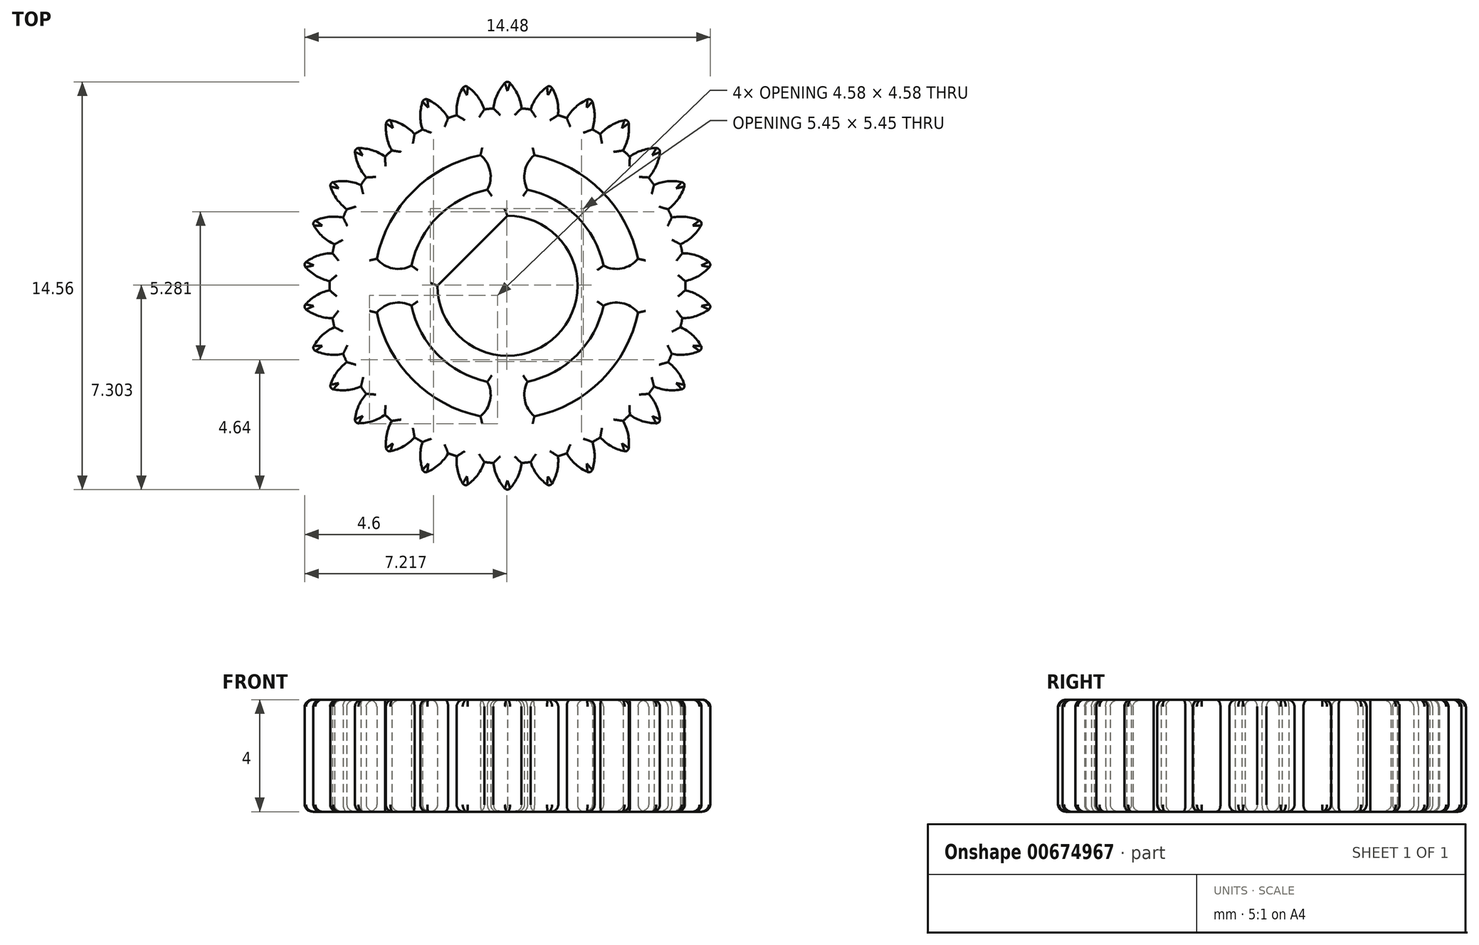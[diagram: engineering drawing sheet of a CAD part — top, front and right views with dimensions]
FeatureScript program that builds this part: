
annotation { "Feature Type Name" : "Feature", "Feature Type Description" : "" }
export const myFeature = defineFeature(function(context is Context, id is Id, definition is map)
    precondition{}
    {
        {
            var Q0;
            Q0=qCreatedBy(makeId("Top.planeOp"),FACE);
            var sketch = newSketch(context, id + "F0", { "sketchPlane" : qUnion([Q0])});
            skCircle(sketch, "E0", {"center": v(0, 0) * mm, "radius": 6.35 * mm});
            skCircle(sketch, "E1", {"center": v(0, 0) * mm, "radius": 4.76 * mm});
            skCircle(sketch, "E2", {"center": v(0, 0) * mm, "radius": 2.5 * mm});
            skCircle(sketch, "E3", {"center": v(0, 0) * mm, "radius": 3.5 * mm});
            skArc(sketch, "E4", {"start": v(-0.72, 3.43) * mm, "mid": v(-0.62, 4.09) * mm, "end": v(-0.96, 4.66) * mm});
            skLineSegment(sketch, "E5", {"start": v(0, 4.76) * mm, "end": v(0, 3.5) * mm});
            skArc(sketch, "E6.MirrorCS", {"start": v(0.72, 3.43) * mm, "mid": v(0.62, 4.09) * mm, "end": v(0.96, 4.66) * mm});
            skArc(sketch, "E7.1.0", {"start": v(-3.43, -0.72) * mm, "mid": v(-4.09, -0.62) * mm, "end": v(-4.66, -0.96) * mm});
            skArc(sketch, "E7.1.1", {"start": v(-3.43, 0.72) * mm, "mid": v(-4.09, 0.62) * mm, "end": v(-4.66, 0.96) * mm});
            skArc(sketch, "E7.2.0", {"start": v(0.72, -3.43) * mm, "mid": v(0.62, -4.09) * mm, "end": v(0.96, -4.66) * mm});
            skArc(sketch, "E7.2.1", {"start": v(-0.72, -3.43) * mm, "mid": v(-0.62, -4.09) * mm, "end": v(-0.96, -4.66) * mm});
            skArc(sketch, "E7.3.0", {"start": v(3.43, 0.72) * mm, "mid": v(4.09, 0.62) * mm, "end": v(4.66, 0.96) * mm});
            skArc(sketch, "E7.3.1", {"start": v(3.43, -0.72) * mm, "mid": v(4.09, -0.62) * mm, "end": v(4.66, -0.96) * mm});
            skLineSegment(sketch, "E8", {"start": v(0, 2.5) * mm, "end": v(-2.5, 0) * mm});
            skLineSegment(sketch, "E9", {"start": v(0, 7.33) * mm, "end": v(-0.5, 6.33) * mm});
            skLineSegment(sketch, "E10", {"start": v(0, 7.33) * mm, "end": v(0.5, 6.33) * mm});
            skArc(sketch, "E11", {"start": v(0, 7.33) * mm, "mid": v(-0.34, 6.88) * mm, "end": v(-0.5, 6.33) * mm});
            skLineSegment(sketch, "E12", {"start": v(0, 7.33) * mm, "end": v(0, 6.35) * mm});
            skArc(sketch, "E13.MirrorCS", {"start": v(0, 7.33) * mm, "mid": v(0.34, 6.88) * mm, "end": v(0.5, 6.33) * mm});
            skLineSegment(sketch, "E14.1.0", {"start": v(-1.52, 7.17) * mm, "end": v(-1.8, 6.09) * mm});
            skLineSegment(sketch, "E14.1.1", {"start": v(-1.52, 7.17) * mm, "end": v(-0.83, 6.3) * mm});
            skArc(sketch, "E14.1.2", {"start": v(-1.52, 7.17) * mm, "mid": v(-1.76, 6.65) * mm, "end": v(-1.8, 6.09) * mm});
            skArc(sketch, "E14.1.3", {"start": v(-1.52, 7.17) * mm, "mid": v(-1.1, 6.8) * mm, "end": v(-0.83, 6.3) * mm});
            skLineSegment(sketch, "E14.2.0", {"start": v(-2.98, 6.7) * mm, "end": v(-3.03, 5.58) * mm});
            skLineSegment(sketch, "E14.2.1", {"start": v(-2.98, 6.7) * mm, "end": v(-2.12, 5.99) * mm});
            skArc(sketch, "E14.2.2", {"start": v(-2.98, 6.7) * mm, "mid": v(-3.1, 6.14) * mm, "end": v(-3.03, 5.58) * mm});
            skArc(sketch, "E14.2.3", {"start": v(-2.98, 6.7) * mm, "mid": v(-2.49, 6.42) * mm, "end": v(-2.12, 5.99) * mm});
            skLineSegment(sketch, "E14.3.0", {"start": v(-4.3, 5.93) * mm, "end": v(-4.13, 4.83) * mm});
            skLineSegment(sketch, "E14.3.1", {"start": v(-4.3, 5.93) * mm, "end": v(-3.32, 5.42) * mm});
            skArc(sketch, "E14.3.2", {"start": v(-4.3, 5.93) * mm, "mid": v(-4.32, 5.36) * mm, "end": v(-4.13, 4.83) * mm});
            skArc(sketch, "E14.3.3", {"start": v(-4.3, 5.93) * mm, "mid": v(-3.77, 5.76) * mm, "end": v(-3.32, 5.42) * mm});
            skLineSegment(sketch, "E14.4.0", {"start": v(-5.45, 4.9) * mm, "end": v(-5.04, 3.86) * mm});
            skLineSegment(sketch, "E14.4.1", {"start": v(-5.45, 4.9) * mm, "end": v(-4.37, 4.6) * mm});
            skArc(sketch, "E14.4.2", {"start": v(-5.45, 4.9) * mm, "mid": v(-5.34, 4.35) * mm, "end": v(-5.04, 3.86) * mm});
            skArc(sketch, "E14.4.3", {"start": v(-5.45, 4.9) * mm, "mid": v(-4.88, 4.85) * mm, "end": v(-4.37, 4.6) * mm});
            skLineSegment(sketch, "E14.5.0", {"start": v(-6.35, 3.67) * mm, "end": v(-5.73, 2.73) * mm});
            skLineSegment(sketch, "E14.5.1", {"start": v(-6.35, 3.67) * mm, "end": v(-5.23, 3.6) * mm});
            skArc(sketch, "E14.5.2", {"start": v(-6.35, 3.67) * mm, "mid": v(-6.13, 3.14) * mm, "end": v(-5.73, 2.73) * mm});
            skArc(sketch, "E14.5.3", {"start": v(-6.35, 3.67) * mm, "mid": v(-5.78, 3.73) * mm, "end": v(-5.23, 3.6) * mm});
            skLineSegment(sketch, "E14.6.0", {"start": v(-6.97, 2.27) * mm, "end": v(-6.17, 1.48) * mm});
            skLineSegment(sketch, "E14.6.1", {"start": v(-6.97, 2.27) * mm, "end": v(-5.87, 2.43) * mm});
            skArc(sketch, "E14.6.2", {"start": v(-6.97, 2.27) * mm, "mid": v(-6.64, 1.8) * mm, "end": v(-6.17, 1.48) * mm});
            skArc(sketch, "E14.6.3", {"start": v(-6.97, 2.27) * mm, "mid": v(-6.43, 2.45) * mm, "end": v(-5.87, 2.43) * mm});
            skLineSegment(sketch, "E14.7.0", {"start": v(-7.3, 0.77) * mm, "end": v(-6.35, 0.16) * mm});
            skLineSegment(sketch, "E14.7.1", {"start": v(-7.3, 0.77) * mm, "end": v(-6.24, 1.16) * mm});
            skArc(sketch, "E14.7.2", {"start": v(-7.3, 0.77) * mm, "mid": v(-6.87, 0.38) * mm, "end": v(-6.35, 0.16) * mm});
            skArc(sketch, "E14.7.3", {"start": v(-7.3, 0.77) * mm, "mid": v(-6.8, 1.06) * mm, "end": v(-6.24, 1.16) * mm});
            skLineSegment(sketch, "E14.8.0", {"start": v(-7.3, -0.77) * mm, "end": v(-6.24, -1.16) * mm});
            skLineSegment(sketch, "E14.8.1", {"start": v(-7.3, -0.77) * mm, "end": v(-6.35, -0.16) * mm});
            skArc(sketch, "E14.8.2", {"start": v(-7.3, -0.77) * mm, "mid": v(-6.8, -1.06) * mm, "end": v(-6.24, -1.16) * mm});
            skArc(sketch, "E14.8.3", {"start": v(-7.3, -0.77) * mm, "mid": v(-6.87, -0.38) * mm, "end": v(-6.35, -0.16) * mm});
            skLineSegment(sketch, "E14.9.0", {"start": v(-6.97, -2.27) * mm, "end": v(-5.87, -2.43) * mm});
            skLineSegment(sketch, "E14.9.1", {"start": v(-6.97, -2.27) * mm, "end": v(-6.17, -1.48) * mm});
            skArc(sketch, "E14.9.2", {"start": v(-6.97, -2.27) * mm, "mid": v(-6.43, -2.45) * mm, "end": v(-5.87, -2.43) * mm});
            skArc(sketch, "E14.9.3", {"start": v(-6.97, -2.27) * mm, "mid": v(-6.64, -1.8) * mm, "end": v(-6.17, -1.48) * mm});
            skLineSegment(sketch, "E14.10.0", {"start": v(-6.35, -3.67) * mm, "end": v(-5.23, -3.6) * mm});
            skLineSegment(sketch, "E14.10.1", {"start": v(-6.35, -3.67) * mm, "end": v(-5.73, -2.73) * mm});
            skArc(sketch, "E14.10.2", {"start": v(-6.35, -3.67) * mm, "mid": v(-5.78, -3.73) * mm, "end": v(-5.23, -3.6) * mm});
            skArc(sketch, "E14.10.3", {"start": v(-6.35, -3.67) * mm, "mid": v(-6.13, -3.14) * mm, "end": v(-5.73, -2.73) * mm});
            skLineSegment(sketch, "E14.11.0", {"start": v(-5.45, -4.9) * mm, "end": v(-4.37, -4.6) * mm});
            skLineSegment(sketch, "E14.11.1", {"start": v(-5.45, -4.9) * mm, "end": v(-5.04, -3.86) * mm});
            skArc(sketch, "E14.11.2", {"start": v(-5.45, -4.9) * mm, "mid": v(-4.88, -4.85) * mm, "end": v(-4.37, -4.6) * mm});
            skArc(sketch, "E14.11.3", {"start": v(-5.45, -4.9) * mm, "mid": v(-5.34, -4.35) * mm, "end": v(-5.04, -3.86) * mm});
            skLineSegment(sketch, "E14.12.0", {"start": v(-4.3, -5.93) * mm, "end": v(-3.32, -5.42) * mm});
            skLineSegment(sketch, "E14.12.1", {"start": v(-4.3, -5.93) * mm, "end": v(-4.13, -4.83) * mm});
            skArc(sketch, "E14.12.2", {"start": v(-4.3, -5.93) * mm, "mid": v(-3.77, -5.76) * mm, "end": v(-3.32, -5.42) * mm});
            skArc(sketch, "E14.12.3", {"start": v(-4.3, -5.93) * mm, "mid": v(-4.32, -5.36) * mm, "end": v(-4.13, -4.83) * mm});
            skLineSegment(sketch, "E14.13.0", {"start": v(-2.98, -6.7) * mm, "end": v(-2.12, -5.99) * mm});
            skLineSegment(sketch, "E14.13.1", {"start": v(-2.98, -6.7) * mm, "end": v(-3.03, -5.58) * mm});
            skArc(sketch, "E14.13.2", {"start": v(-2.98, -6.7) * mm, "mid": v(-2.49, -6.42) * mm, "end": v(-2.12, -5.99) * mm});
            skArc(sketch, "E14.13.3", {"start": v(-2.98, -6.7) * mm, "mid": v(-3.1, -6.14) * mm, "end": v(-3.03, -5.58) * mm});
            skLineSegment(sketch, "E14.14.0", {"start": v(-1.52, -7.17) * mm, "end": v(-0.83, -6.3) * mm});
            skLineSegment(sketch, "E14.14.1", {"start": v(-1.52, -7.17) * mm, "end": v(-1.8, -6.09) * mm});
            skArc(sketch, "E14.14.2", {"start": v(-1.52, -7.17) * mm, "mid": v(-1.1, -6.8) * mm, "end": v(-0.83, -6.3) * mm});
            skArc(sketch, "E14.14.3", {"start": v(-1.52, -7.17) * mm, "mid": v(-1.76, -6.65) * mm, "end": v(-1.8, -6.09) * mm});
            skLineSegment(sketch, "E14.15.0", {"start": v(0, -7.33) * mm, "end": v(0.5, -6.33) * mm});
            skLineSegment(sketch, "E14.15.1", {"start": v(0, -7.33) * mm, "end": v(-0.5, -6.33) * mm});
            skArc(sketch, "E14.15.2", {"start": v(0, -7.33) * mm, "mid": v(0.34, -6.88) * mm, "end": v(0.5, -6.33) * mm});
            skArc(sketch, "E14.15.3", {"start": v(0, -7.33) * mm, "mid": v(-0.34, -6.88) * mm, "end": v(-0.5, -6.33) * mm});
            skLineSegment(sketch, "E14.16.0", {"start": v(1.52, -7.17) * mm, "end": v(1.8, -6.09) * mm});
            skLineSegment(sketch, "E14.16.1", {"start": v(1.52, -7.17) * mm, "end": v(0.83, -6.3) * mm});
            skArc(sketch, "E14.16.2", {"start": v(1.52, -7.17) * mm, "mid": v(1.76, -6.65) * mm, "end": v(1.8, -6.09) * mm});
            skArc(sketch, "E14.16.3", {"start": v(1.52, -7.17) * mm, "mid": v(1.1, -6.8) * mm, "end": v(0.83, -6.3) * mm});
            skLineSegment(sketch, "E14.17.0", {"start": v(2.98, -6.7) * mm, "end": v(3.03, -5.58) * mm});
            skLineSegment(sketch, "E14.17.1", {"start": v(2.98, -6.7) * mm, "end": v(2.12, -5.99) * mm});
            skArc(sketch, "E14.17.2", {"start": v(2.98, -6.7) * mm, "mid": v(3.1, -6.14) * mm, "end": v(3.03, -5.58) * mm});
            skArc(sketch, "E14.17.3", {"start": v(2.98, -6.7) * mm, "mid": v(2.49, -6.42) * mm, "end": v(2.12, -5.99) * mm});
            skLineSegment(sketch, "E14.18.0", {"start": v(4.3, -5.93) * mm, "end": v(4.13, -4.83) * mm});
            skLineSegment(sketch, "E14.18.1", {"start": v(4.3, -5.93) * mm, "end": v(3.32, -5.42) * mm});
            skArc(sketch, "E14.18.2", {"start": v(4.3, -5.93) * mm, "mid": v(4.32, -5.36) * mm, "end": v(4.13, -4.83) * mm});
            skArc(sketch, "E14.18.3", {"start": v(4.3, -5.93) * mm, "mid": v(3.77, -5.76) * mm, "end": v(3.32, -5.42) * mm});
            skLineSegment(sketch, "E14.19.0", {"start": v(5.45, -4.9) * mm, "end": v(5.04, -3.86) * mm});
            skLineSegment(sketch, "E14.19.1", {"start": v(5.45, -4.9) * mm, "end": v(4.37, -4.6) * mm});
            skArc(sketch, "E14.19.2", {"start": v(5.45, -4.9) * mm, "mid": v(5.34, -4.35) * mm, "end": v(5.04, -3.86) * mm});
            skArc(sketch, "E14.19.3", {"start": v(5.45, -4.9) * mm, "mid": v(4.88, -4.85) * mm, "end": v(4.37, -4.6) * mm});
            skLineSegment(sketch, "E14.20.0", {"start": v(6.35, -3.67) * mm, "end": v(5.73, -2.73) * mm});
            skLineSegment(sketch, "E14.20.1", {"start": v(6.35, -3.67) * mm, "end": v(5.23, -3.6) * mm});
            skArc(sketch, "E14.20.2", {"start": v(6.35, -3.67) * mm, "mid": v(6.13, -3.14) * mm, "end": v(5.73, -2.73) * mm});
            skArc(sketch, "E14.20.3", {"start": v(6.35, -3.67) * mm, "mid": v(5.78, -3.73) * mm, "end": v(5.23, -3.6) * mm});
            skLineSegment(sketch, "E14.21.0", {"start": v(6.97, -2.27) * mm, "end": v(6.17, -1.48) * mm});
            skLineSegment(sketch, "E14.21.1", {"start": v(6.97, -2.27) * mm, "end": v(5.87, -2.43) * mm});
            skArc(sketch, "E14.21.2", {"start": v(6.97, -2.27) * mm, "mid": v(6.64, -1.8) * mm, "end": v(6.17, -1.48) * mm});
            skArc(sketch, "E14.21.3", {"start": v(6.97, -2.27) * mm, "mid": v(6.43, -2.45) * mm, "end": v(5.87, -2.43) * mm});
            skLineSegment(sketch, "E14.22.0", {"start": v(7.3, -0.77) * mm, "end": v(6.35, -0.16) * mm});
            skLineSegment(sketch, "E14.22.1", {"start": v(7.3, -0.77) * mm, "end": v(6.24, -1.16) * mm});
            skArc(sketch, "E14.22.2", {"start": v(7.3, -0.77) * mm, "mid": v(6.87, -0.38) * mm, "end": v(6.35, -0.16) * mm});
            skArc(sketch, "E14.22.3", {"start": v(7.3, -0.77) * mm, "mid": v(6.8, -1.06) * mm, "end": v(6.24, -1.16) * mm});
            skLineSegment(sketch, "E14.23.0", {"start": v(7.3, 0.77) * mm, "end": v(6.24, 1.16) * mm});
            skLineSegment(sketch, "E14.23.1", {"start": v(7.3, 0.77) * mm, "end": v(6.35, 0.16) * mm});
            skArc(sketch, "E14.23.2", {"start": v(7.3, 0.77) * mm, "mid": v(6.8, 1.06) * mm, "end": v(6.24, 1.16) * mm});
            skArc(sketch, "E14.23.3", {"start": v(7.3, 0.77) * mm, "mid": v(6.87, 0.38) * mm, "end": v(6.35, 0.16) * mm});
            skLineSegment(sketch, "E14.24.0", {"start": v(6.97, 2.27) * mm, "end": v(5.87, 2.43) * mm});
            skLineSegment(sketch, "E14.24.1", {"start": v(6.97, 2.27) * mm, "end": v(6.17, 1.48) * mm});
            skArc(sketch, "E14.24.2", {"start": v(6.97, 2.27) * mm, "mid": v(6.43, 2.45) * mm, "end": v(5.87, 2.43) * mm});
            skArc(sketch, "E14.24.3", {"start": v(6.97, 2.27) * mm, "mid": v(6.64, 1.8) * mm, "end": v(6.17, 1.48) * mm});
            skLineSegment(sketch, "E14.25.0", {"start": v(6.35, 3.67) * mm, "end": v(5.23, 3.6) * mm});
            skLineSegment(sketch, "E14.25.1", {"start": v(6.35, 3.67) * mm, "end": v(5.73, 2.73) * mm});
            skArc(sketch, "E14.25.2", {"start": v(6.35, 3.67) * mm, "mid": v(5.78, 3.73) * mm, "end": v(5.23, 3.6) * mm});
            skArc(sketch, "E14.25.3", {"start": v(6.35, 3.67) * mm, "mid": v(6.13, 3.14) * mm, "end": v(5.73, 2.73) * mm});
            skLineSegment(sketch, "E14.26.0", {"start": v(5.45, 4.9) * mm, "end": v(4.37, 4.6) * mm});
            skLineSegment(sketch, "E14.26.1", {"start": v(5.45, 4.9) * mm, "end": v(5.04, 3.86) * mm});
            skArc(sketch, "E14.26.2", {"start": v(5.45, 4.9) * mm, "mid": v(4.88, 4.85) * mm, "end": v(4.37, 4.6) * mm});
            skArc(sketch, "E14.26.3", {"start": v(5.45, 4.9) * mm, "mid": v(5.34, 4.35) * mm, "end": v(5.04, 3.86) * mm});
            skLineSegment(sketch, "E14.27.0", {"start": v(4.3, 5.93) * mm, "end": v(3.32, 5.42) * mm});
            skLineSegment(sketch, "E14.27.1", {"start": v(4.3, 5.93) * mm, "end": v(4.13, 4.83) * mm});
            skArc(sketch, "E14.27.2", {"start": v(4.3, 5.93) * mm, "mid": v(3.77, 5.76) * mm, "end": v(3.32, 5.42) * mm});
            skArc(sketch, "E14.27.3", {"start": v(4.3, 5.93) * mm, "mid": v(4.32, 5.36) * mm, "end": v(4.13, 4.83) * mm});
            skLineSegment(sketch, "E14.28.0", {"start": v(2.98, 6.7) * mm, "end": v(2.12, 5.99) * mm});
            skLineSegment(sketch, "E14.28.1", {"start": v(2.98, 6.7) * mm, "end": v(3.03, 5.58) * mm});
            skArc(sketch, "E14.28.2", {"start": v(2.98, 6.7) * mm, "mid": v(2.49, 6.42) * mm, "end": v(2.12, 5.99) * mm});
            skArc(sketch, "E14.28.3", {"start": v(2.98, 6.7) * mm, "mid": v(3.1, 6.14) * mm, "end": v(3.03, 5.58) * mm});
            skLineSegment(sketch, "E14.29.0", {"start": v(1.52, 7.17) * mm, "end": v(0.83, 6.3) * mm});
            skLineSegment(sketch, "E14.29.1", {"start": v(1.52, 7.17) * mm, "end": v(1.8, 6.09) * mm});
            skArc(sketch, "E14.29.2", {"start": v(1.52, 7.17) * mm, "mid": v(1.1, 6.8) * mm, "end": v(0.83, 6.3) * mm});
            skArc(sketch, "E14.29.3", {"start": v(1.52, 7.17) * mm, "mid": v(1.76, 6.65) * mm, "end": v(1.8, 6.09) * mm});
            skSolve(sketch);
        }
        {
            var Q0;
            Q0=qSketchRegion(id+"F0",true);
            var Q1;
            {var subQ0=sQuery(id+"F0.wireOp",EDGE,"E4");Q1=makeQuery(id+"F0.imprint","IMPRINT",FACE,{"disambiguationData":[TD([[makeQuery(id+"F0.imprint","IMPRINT",EDGE,{"derivedFrom":subQ0}),-1.0]])]});}
            var Q2;
            {var subQ0=sQuery(id+"F0.wireOp",EDGE,"E5");Q2=makeQuery(id+"F0.imprint","IMPRINT",FACE,{"disambiguationData":[TD([[makeQuery(id+"F0.imprint","IMPRINT",EDGE,{"derivedFrom":subQ0}),1.0]])]});}
            var Q3;
            {var subQ0=sQuery(id+"F0.wireOp",EDGE,"E7.1.0");Q3=makeQuery(id+"F0.imprint","IMPRINT",FACE,{"disambiguationData":[TD([[makeQuery(id+"F0.imprint","IMPRINT",EDGE,{"derivedFrom":subQ0}),-1.0]])]});}
            var Q4;
            {var subQ0=sQuery(id+"F0.wireOp",EDGE,"E7.3.0");Q4=makeQuery(id+"F0.imprint","IMPRINT",FACE,{"disambiguationData":[TD([[makeQuery(id+"F0.imprint","IMPRINT",EDGE,{"derivedFrom":subQ0}),-1.0]])]});}
            var Q5;
            {var subQ0=sQuery(id+"F0.wireOp",EDGE,"E7.2.0");Q5=makeQuery(id+"F0.imprint","IMPRINT",FACE,{"disambiguationData":[TD([[makeQuery(id+"F0.imprint","IMPRINT",EDGE,{"derivedFrom":subQ0}),-1.0]])]});}
            var Q6;
            {var subQ8=sQuery(id+"F0.wireOp",EDGE,"E8");var subQ9=sQuery(id+"F0.wireOp",EDGE,"E2");var subQ10=makeQuery(id+"F0.imprint","INTERSECT",VERTEX,{"disambiguationData":[OD(0.0)],"derivedFrom":[subQ9,subQ8]});Q6=makeQuery(id+"F0.imprint","IMPRINT",FACE,{"disambiguationData":[TD([[makeQuery(id+"F0.imprint","IMPRINT",EDGE,{"disambiguationData":[TD([[subQ10,-1.0]])],"derivedFrom":subQ9}),-1.0]])]});}
            var Q7;
            {var subQ0=sQuery(id+"F0.wireOp",EDGE,"E8");Q7=makeQuery(id+"F0.imprint","IMPRINT",FACE,{"disambiguationData":[TD([[makeQuery(id+"F0.imprint","IMPRINT",EDGE,{"derivedFrom":subQ0}),-1.0]])]});}
            extrude(context, id + "F1", {"entities" : qUnion([Q0, Q1, Q2, Q3, Q4, Q5, Q6, Q7]), "depth" : 4 * mm, "offsetDistance" : 25.4 * mm});
        }
        {
            var Q0;
            Q0=makeQuery(id+"F1.opExtrude","CAP_FACE",FACE,{"disambiguationData":[OSD([sQuery(id+"F0.wireOp",EDGE,"E0"),sQuery(id+"F0.wireOp",EDGE,"E1"),sQuery(id+"F0.wireOp",EDGE,"E2"),sQuery(id+"F0.wireOp",EDGE,"E3"),sQuery(id+"F0.wireOp",EDGE,"E4"),sQuery(id+"F0.wireOp",EDGE,"E6.MirrorCS"),sQuery(id+"F0.wireOp",EDGE,"E7.1.0"),sQuery(id+"F0.wireOp",EDGE,"E7.1.1"),sQuery(id+"F0.wireOp",EDGE,"E7.2.0"),sQuery(id+"F0.wireOp",EDGE,"E7.2.1"),sQuery(id+"F0.wireOp",EDGE,"E7.3.0"),sQuery(id+"F0.wireOp",EDGE,"E7.3.1"),sQuery(id+"F0.wireOp",EDGE,"E8")])],"isStart":false});
            var Q1;
            Q1=makeQuery(id+"F1.opExtrude","CAP_FACE",FACE,{"disambiguationData":[OSD([sQuery(id+"F0.wireOp",EDGE,"E0"),sQuery(id+"F0.wireOp",EDGE,"E1"),sQuery(id+"F0.wireOp",EDGE,"E2"),sQuery(id+"F0.wireOp",EDGE,"E3"),sQuery(id+"F0.wireOp",EDGE,"E4"),sQuery(id+"F0.wireOp",EDGE,"E6.MirrorCS"),sQuery(id+"F0.wireOp",EDGE,"E7.1.0"),sQuery(id+"F0.wireOp",EDGE,"E7.1.1"),sQuery(id+"F0.wireOp",EDGE,"E7.2.0"),sQuery(id+"F0.wireOp",EDGE,"E7.2.1"),sQuery(id+"F0.wireOp",EDGE,"E7.3.0"),sQuery(id+"F0.wireOp",EDGE,"E7.3.1"),sQuery(id+"F0.wireOp",EDGE,"E8")])],"isStart":true});
            fillet(context, id + "F2", {"entities" : qUnion([Q0, Q1]), "radius" : 0.25 * mm, "tangentPropagation" : true, "allowEdgeOverflow" : false});
        }
        {
            var Q0;
            Q0=makeQuery(id+"F1.opExtrude","SWEPT_EDGE",EDGE,{"disambiguationData":[OSD([sQuery(id+"F0.wireOp",EDGE,"E9"),sQuery(id+"F0.wireOp",EDGE,"E10"),sQuery(id+"F0.wireOp",EDGE,"E11"),sQuery(id+"F0.wireOp",EDGE,"E12"),sQuery(id+"F0.wireOp",EDGE,"E13.MirrorCS")])]});
            var Q1;
            Q1=makeQuery(id+"F1.opExtrude","SWEPT_EDGE",EDGE,{"disambiguationData":[OSD([sQuery(id+"F0.wireOp",EDGE,"E14.1.0"),sQuery(id+"F0.wireOp",EDGE,"E14.1.1"),sQuery(id+"F0.wireOp",EDGE,"E14.1.2"),sQuery(id+"F0.wireOp",EDGE,"E14.1.3")])]});
            var Q2;
            Q2=makeQuery(id+"F1.opExtrude","SWEPT_EDGE",EDGE,{"disambiguationData":[OSD([sQuery(id+"F0.wireOp",EDGE,"E14.29.0"),sQuery(id+"F0.wireOp",EDGE,"E14.29.1"),sQuery(id+"F0.wireOp",EDGE,"E14.29.2"),sQuery(id+"F0.wireOp",EDGE,"E14.29.3")])]});
            var Q3;
            Q3=makeQuery(id+"F1.opExtrude","SWEPT_EDGE",EDGE,{"disambiguationData":[OSD([sQuery(id+"F0.wireOp",EDGE,"E14.28.0"),sQuery(id+"F0.wireOp",EDGE,"E14.28.1"),sQuery(id+"F0.wireOp",EDGE,"E14.28.2"),sQuery(id+"F0.wireOp",EDGE,"E14.28.3")])]});
            var Q4;
            Q4=makeQuery(id+"F1.opExtrude","SWEPT_EDGE",EDGE,{"disambiguationData":[OSD([sQuery(id+"F0.wireOp",EDGE,"E14.2.0"),sQuery(id+"F0.wireOp",EDGE,"E14.2.1"),sQuery(id+"F0.wireOp",EDGE,"E14.2.2"),sQuery(id+"F0.wireOp",EDGE,"E14.2.3")])]});
            var Q5;
            Q5=makeQuery(id+"F1.opExtrude","SWEPT_EDGE",EDGE,{"disambiguationData":[OSD([sQuery(id+"F0.wireOp",EDGE,"E14.3.0"),sQuery(id+"F0.wireOp",EDGE,"E14.3.1"),sQuery(id+"F0.wireOp",EDGE,"E14.3.2"),sQuery(id+"F0.wireOp",EDGE,"E14.3.3")])]});
            var Q6;
            Q6=makeQuery(id+"F1.opExtrude","SWEPT_EDGE",EDGE,{"disambiguationData":[OSD([sQuery(id+"F0.wireOp",EDGE,"E14.4.0"),sQuery(id+"F0.wireOp",EDGE,"E14.4.1"),sQuery(id+"F0.wireOp",EDGE,"E14.4.2"),sQuery(id+"F0.wireOp",EDGE,"E14.4.3")])]});
            var Q7;
            Q7=makeQuery(id+"F1.opExtrude","SWEPT_EDGE",EDGE,{"disambiguationData":[OSD([sQuery(id+"F0.wireOp",EDGE,"E14.5.0"),sQuery(id+"F0.wireOp",EDGE,"E14.5.1"),sQuery(id+"F0.wireOp",EDGE,"E14.5.2"),sQuery(id+"F0.wireOp",EDGE,"E14.5.3")])]});
            var Q8;
            Q8=makeQuery(id+"F1.opExtrude","SWEPT_EDGE",EDGE,{"disambiguationData":[OSD([sQuery(id+"F0.wireOp",EDGE,"E14.6.0"),sQuery(id+"F0.wireOp",EDGE,"E14.6.1"),sQuery(id+"F0.wireOp",EDGE,"E14.6.2"),sQuery(id+"F0.wireOp",EDGE,"E14.6.3")])]});
            var Q9;
            Q9=makeQuery(id+"F1.opExtrude","SWEPT_EDGE",EDGE,{"disambiguationData":[OSD([sQuery(id+"F0.wireOp",EDGE,"E14.27.0"),sQuery(id+"F0.wireOp",EDGE,"E14.27.1"),sQuery(id+"F0.wireOp",EDGE,"E14.27.2"),sQuery(id+"F0.wireOp",EDGE,"E14.27.3")])]});
            var Q10;
            Q10=makeQuery(id+"F1.opExtrude","SWEPT_EDGE",EDGE,{"disambiguationData":[OSD([sQuery(id+"F0.wireOp",EDGE,"E14.26.0"),sQuery(id+"F0.wireOp",EDGE,"E14.26.1"),sQuery(id+"F0.wireOp",EDGE,"E14.26.2"),sQuery(id+"F0.wireOp",EDGE,"E14.26.3")])]});
            var Q11;
            Q11=makeQuery(id+"F1.opExtrude","SWEPT_EDGE",EDGE,{"disambiguationData":[OSD([sQuery(id+"F0.wireOp",EDGE,"E14.25.0"),sQuery(id+"F0.wireOp",EDGE,"E14.25.1"),sQuery(id+"F0.wireOp",EDGE,"E14.25.2"),sQuery(id+"F0.wireOp",EDGE,"E14.25.3")])]});
            var Q12;
            Q12=makeQuery(id+"F1.opExtrude","SWEPT_EDGE",EDGE,{"disambiguationData":[OSD([sQuery(id+"F0.wireOp",EDGE,"E14.24.0"),sQuery(id+"F0.wireOp",EDGE,"E14.24.1"),sQuery(id+"F0.wireOp",EDGE,"E14.24.2"),sQuery(id+"F0.wireOp",EDGE,"E14.24.3")])]});
            var Q13;
            Q13=makeQuery(id+"F1.opExtrude","SWEPT_EDGE",EDGE,{"disambiguationData":[OSD([sQuery(id+"F0.wireOp",EDGE,"E14.23.0"),sQuery(id+"F0.wireOp",EDGE,"E14.23.1"),sQuery(id+"F0.wireOp",EDGE,"E14.23.2"),sQuery(id+"F0.wireOp",EDGE,"E14.23.3")])]});
            var Q14;
            Q14=makeQuery(id+"F1.opExtrude","SWEPT_EDGE",EDGE,{"disambiguationData":[OSD([sQuery(id+"F0.wireOp",EDGE,"E14.22.0"),sQuery(id+"F0.wireOp",EDGE,"E14.22.1"),sQuery(id+"F0.wireOp",EDGE,"E14.22.2"),sQuery(id+"F0.wireOp",EDGE,"E14.22.3")])]});
            var Q15;
            Q15=makeQuery(id+"F1.opExtrude","SWEPT_EDGE",EDGE,{"disambiguationData":[OSD([sQuery(id+"F0.wireOp",EDGE,"E14.21.0"),sQuery(id+"F0.wireOp",EDGE,"E14.21.1"),sQuery(id+"F0.wireOp",EDGE,"E14.21.2"),sQuery(id+"F0.wireOp",EDGE,"E14.21.3")])]});
            var Q16;
            Q16=makeQuery(id+"F1.opExtrude","SWEPT_EDGE",EDGE,{"disambiguationData":[OSD([sQuery(id+"F0.wireOp",EDGE,"E14.20.0"),sQuery(id+"F0.wireOp",EDGE,"E14.20.1"),sQuery(id+"F0.wireOp",EDGE,"E14.20.2"),sQuery(id+"F0.wireOp",EDGE,"E14.20.3")])]});
            var Q17;
            Q17=makeQuery(id+"F1.opExtrude","SWEPT_EDGE",EDGE,{"disambiguationData":[OSD([sQuery(id+"F0.wireOp",EDGE,"E14.7.0"),sQuery(id+"F0.wireOp",EDGE,"E14.7.1"),sQuery(id+"F0.wireOp",EDGE,"E14.7.2"),sQuery(id+"F0.wireOp",EDGE,"E14.7.3")])]});
            var Q18;
            Q18=makeQuery(id+"F1.opExtrude","SWEPT_EDGE",EDGE,{"disambiguationData":[OSD([sQuery(id+"F0.wireOp",EDGE,"E14.8.0"),sQuery(id+"F0.wireOp",EDGE,"E14.8.1"),sQuery(id+"F0.wireOp",EDGE,"E14.8.2"),sQuery(id+"F0.wireOp",EDGE,"E14.8.3")])]});
            var Q19;
            Q19=makeQuery(id+"F1.opExtrude","SWEPT_EDGE",EDGE,{"disambiguationData":[OSD([sQuery(id+"F0.wireOp",EDGE,"E14.9.0"),sQuery(id+"F0.wireOp",EDGE,"E14.9.1"),sQuery(id+"F0.wireOp",EDGE,"E14.9.2"),sQuery(id+"F0.wireOp",EDGE,"E14.9.3")])]});
            var Q20;
            Q20=makeQuery(id+"F1.opExtrude","SWEPT_EDGE",EDGE,{"disambiguationData":[OSD([sQuery(id+"F0.wireOp",EDGE,"E14.10.0"),sQuery(id+"F0.wireOp",EDGE,"E14.10.1"),sQuery(id+"F0.wireOp",EDGE,"E14.10.2"),sQuery(id+"F0.wireOp",EDGE,"E14.10.3")])]});
            var Q21;
            Q21=makeQuery(id+"F1.opExtrude","SWEPT_EDGE",EDGE,{"disambiguationData":[OSD([sQuery(id+"F0.wireOp",EDGE,"E14.11.0"),sQuery(id+"F0.wireOp",EDGE,"E14.11.1"),sQuery(id+"F0.wireOp",EDGE,"E14.11.2"),sQuery(id+"F0.wireOp",EDGE,"E14.11.3")])]});
            var Q22;
            Q22=makeQuery(id+"F1.opExtrude","SWEPT_EDGE",EDGE,{"disambiguationData":[OSD([sQuery(id+"F0.wireOp",EDGE,"E14.13.0"),sQuery(id+"F0.wireOp",EDGE,"E14.13.1"),sQuery(id+"F0.wireOp",EDGE,"E14.13.2"),sQuery(id+"F0.wireOp",EDGE,"E14.13.3")])]});
            var Q23;
            Q23=makeQuery(id+"F1.opExtrude","SWEPT_EDGE",EDGE,{"disambiguationData":[OSD([sQuery(id+"F0.wireOp",EDGE,"E14.12.0"),sQuery(id+"F0.wireOp",EDGE,"E14.12.1"),sQuery(id+"F0.wireOp",EDGE,"E14.12.2"),sQuery(id+"F0.wireOp",EDGE,"E14.12.3")])]});
            var Q24;
            Q24=makeQuery(id+"F1.opExtrude","SWEPT_EDGE",EDGE,{"disambiguationData":[OSD([sQuery(id+"F0.wireOp",EDGE,"E14.19.0"),sQuery(id+"F0.wireOp",EDGE,"E14.19.1"),sQuery(id+"F0.wireOp",EDGE,"E14.19.2"),sQuery(id+"F0.wireOp",EDGE,"E14.19.3")])]});
            var Q25;
            Q25=makeQuery(id+"F1.opExtrude","SWEPT_EDGE",EDGE,{"disambiguationData":[OSD([sQuery(id+"F0.wireOp",EDGE,"E14.18.0"),sQuery(id+"F0.wireOp",EDGE,"E14.18.1"),sQuery(id+"F0.wireOp",EDGE,"E14.18.2"),sQuery(id+"F0.wireOp",EDGE,"E14.18.3")])]});
            var Q26;
            Q26=makeQuery(id+"F1.opExtrude","SWEPT_EDGE",EDGE,{"disambiguationData":[OSD([sQuery(id+"F0.wireOp",EDGE,"E14.17.0"),sQuery(id+"F0.wireOp",EDGE,"E14.17.1"),sQuery(id+"F0.wireOp",EDGE,"E14.17.2"),sQuery(id+"F0.wireOp",EDGE,"E14.17.3")])]});
            var Q27;
            Q27=makeQuery(id+"F1.opExtrude","SWEPT_EDGE",EDGE,{"disambiguationData":[OSD([sQuery(id+"F0.wireOp",EDGE,"E14.16.0"),sQuery(id+"F0.wireOp",EDGE,"E14.16.1"),sQuery(id+"F0.wireOp",EDGE,"E14.16.2"),sQuery(id+"F0.wireOp",EDGE,"E14.16.3")])]});
            var Q28;
            Q28=makeQuery(id+"F1.opExtrude","SWEPT_EDGE",EDGE,{"disambiguationData":[OSD([sQuery(id+"F0.wireOp",EDGE,"E14.15.0"),sQuery(id+"F0.wireOp",EDGE,"E14.15.1"),sQuery(id+"F0.wireOp",EDGE,"E14.15.2"),sQuery(id+"F0.wireOp",EDGE,"E14.15.3")])]});
            var Q29;
            Q29=makeQuery(id+"F1.opExtrude","SWEPT_EDGE",EDGE,{"disambiguationData":[OSD([sQuery(id+"F0.wireOp",EDGE,"E14.14.0"),sQuery(id+"F0.wireOp",EDGE,"E14.14.1"),sQuery(id+"F0.wireOp",EDGE,"E14.14.2"),sQuery(id+"F0.wireOp",EDGE,"E14.14.3")])]});
            fillet(context, id + "F3", {"entities" : qUnion([Q0, Q1, Q2, Q3, Q4, Q5, Q6, Q7, Q8, Q9, Q10, Q11, Q12, Q13, Q14, Q15, Q16, Q17, Q18, Q19, Q20, Q21, Q22, Q23, Q24, Q25, Q26, Q27, Q28, Q29]), "radius" : 0.12 * mm, "tangentPropagation" : true, "allowEdgeOverflow" : false});
        }
    });
